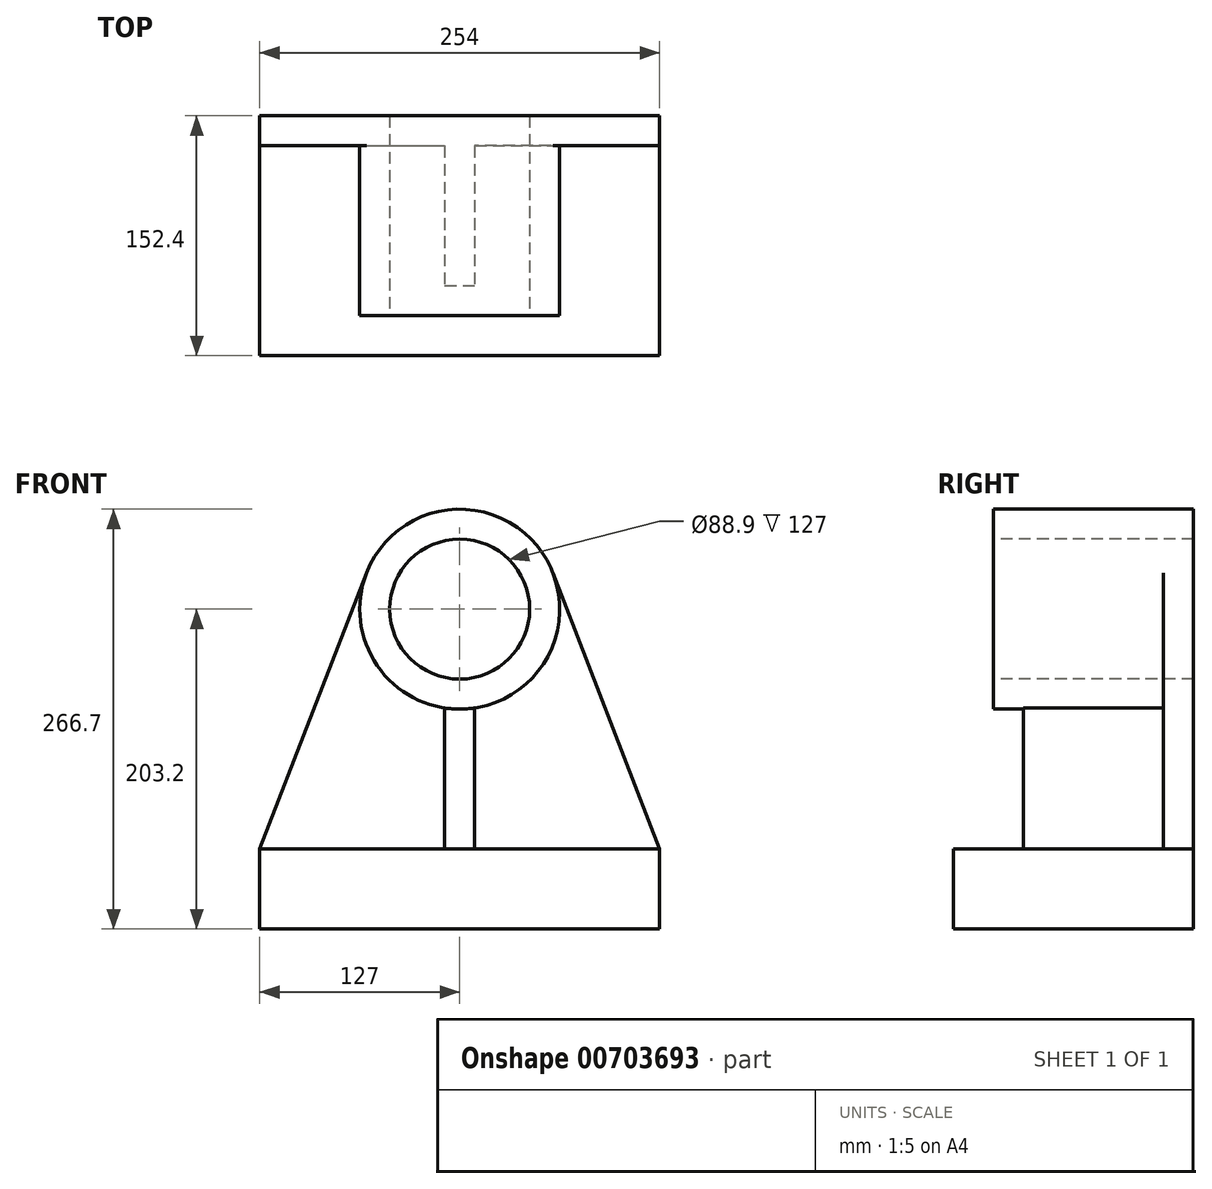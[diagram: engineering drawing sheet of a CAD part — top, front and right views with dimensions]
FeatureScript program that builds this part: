
annotation { "Feature Type Name" : "Feature", "Feature Type Description" : "" }
export const myFeature = defineFeature(function(context is Context, id is Id, definition is map)
    precondition{}
    {
        {
            var Q0;
            Q0=qCreatedBy(makeId("Front.planeOp"),FACE);
            var sketch = newSketch(context, id + "F0", { "sketchPlane" : qUnion([Q0])});
            skLineSegment(sketch, "E0", {"start": v(0, 0) * mm, "end": v(254, 0) * mm});
            skLineSegment(sketch, "E1", {"start": v(254, 0) * mm, "end": v(254, 50.8) * mm});
            skLineSegment(sketch, "E2", {"start": v(254, 50.8) * mm, "end": v(186.23, 226.1) * mm});
            skLineSegment(sketch, "E3", {"start": v(0, 0) * mm, "end": v(0, 50.8) * mm});
            skLineSegment(sketch, "E4", {"start": v(0, 50.8) * mm, "end": v(67.77, 226.1) * mm});
            skArc(sketch, "E5", {"start": v(186.23, 226.1) * mm, "mid": v(127, 266.7) * mm, "end": v(67.77, 226.1) * mm});
            skLineSegment(sketch, "E6", {"start": v(127, 0) * mm, "end": v(127, 266.7) * mm, "construction": true});
            skSolve(sketch);
        }
        {
            var Q0;
            Q0 = qSketchRegion(id + "F0", true);
            extrude(context, id + "F1", {"entities" : qUnion([Q0]), "depth" : 152.4 * mm, "offsetDistance" : 25.4 * mm});
        }
        {
            var Q0;
            Q0=makeQuery(id+"F1.opExtrude","CAP_FACE",FACE,{"disambiguationData":[OSD([sQuery(id+"F0.wireOp",EDGE,"E0"),sQuery(id+"F0.wireOp",EDGE,"E1"),sQuery(id+"F0.wireOp",EDGE,"E2"),sQuery(id+"F0.wireOp",EDGE,"E3"),sQuery(id+"F0.wireOp",EDGE,"E4"),sQuery(id+"F0.wireOp",EDGE,"E5")])],"isStart":false});
            var sketch = newSketch(context, id + "F2", { "sketchPlane" : qUnion([Q0])});
            skLineSegment(sketch, "E7", {"start": v(0, 50.8) * mm, "end": v(117.47, 50.8) * mm});
            skLineSegment(sketch, "E8", {"start": v(117.47, 50.8) * mm, "end": v(117.47, 140.42) * mm});
            skCircle(sketch, "E9", {"center": v(127, 203.2) * mm, "radius": 63.5 * mm});
            skLineSegment(sketch, "E10", {"start": v(254, 50.8) * mm, "end": v(136.53, 50.8) * mm});
            skLineSegment(sketch, "E11", {"start": v(136.53, 50.8) * mm, "end": v(136.53, 140.42) * mm});
            skLineSegment(sketch, "E12", {"start": v(127, 266.7) * mm, "end": v(127, 0) * mm, "construction": true});
            skSolve(sketch);
        }
        {
            var Q0;
            Q0=makeQuery(id+"F2.imprint","IMPRINT",FACE,{"disambiguationData":[TD([[makeQuery(id+"F2.imprint","IMPRINT",EDGE,{"derivedFrom":sQuery(id+"F2.wireOp",EDGE,"E10")}),-1.0]])]});
            var Q1;
            Q1=makeQuery(id+"F2.imprint","IMPRINT",FACE,{"disambiguationData":[TD([[makeQuery(id+"F2.imprint","IMPRINT",EDGE,{"derivedFrom":sQuery(id+"F2.wireOp",EDGE,"E7")}),1.0]])]});
            extrude(context, id + "F3", {"entities" : qUnion([Q0, Q1]), "operationType" : NewBodyOperationType.REMOVE, "oppositeDirection" : true, "depth" : 133.35 * mm, "offsetDistance" : 25.4 * mm});
        }
        {
            var Q0;
            Q0=makeQuery(id+"F1.opExtrude","CAP_FACE",FACE,{"disambiguationData":[OSD([sQuery(id+"F0.wireOp",EDGE,"E0"),sQuery(id+"F0.wireOp",EDGE,"E1"),sQuery(id+"F0.wireOp",EDGE,"E2"),sQuery(id+"F0.wireOp",EDGE,"E3"),sQuery(id+"F0.wireOp",EDGE,"E4"),sQuery(id+"F0.wireOp",EDGE,"E5")])],"isStart":false});
            var sketch = newSketch(context, id + "F4", { "sketchPlane" : qUnion([Q0])});
            skCircle(sketch, "E13", {"center": v(127, 203.2) * mm, "radius": 44.45 * mm});
            skSolve(sketch);
        }
        {
            var Q0;
            Q0 = qSketchRegion(id + "F4", true);
            extrude(context, id + "F5", {"entities" : qUnion([Q0]), "operationType" : NewBodyOperationType.REMOVE, "endBound" : BoundingType.THROUGH_ALL, "oppositeDirection" : true, "depth" : 25.4 * mm, "offsetDistance" : 25.4 * mm});
        }
        {
            var Q0;
            Q0=makeQuery(id+"F1.opExtrude","CAP_FACE",FACE,{"disambiguationData":[OSD([sQuery(id+"F0.wireOp",EDGE,"E0"),sQuery(id+"F0.wireOp",EDGE,"E1"),sQuery(id+"F0.wireOp",EDGE,"E2"),sQuery(id+"F0.wireOp",EDGE,"E3"),sQuery(id+"F0.wireOp",EDGE,"E4"),sQuery(id+"F0.wireOp",EDGE,"E5")])],"isStart":false});
            var sketch = newSketch(context, id + "F6", { "sketchPlane" : qUnion([Q0])});
            skLineSegment(sketch, "E14", {"start": v(117.47, 50.8) * mm, "end": v(136.53, 50.8) * mm});
            skLineSegment(sketch, "E15", {"start": v(136.53, 50.8) * mm, "end": v(136.53, 140.42) * mm});
            skArc(sketch, "E16", {"start": v(117.47, 140.42) * mm, "mid": v(127, 139.7) * mm, "end": v(136.53, 140.42) * mm});
            skLineSegment(sketch, "E17", {"start": v(117.47, 140.42) * mm, "end": v(117.47, 50.8) * mm});
            skSolve(sketch);
        }
        {
            var Q0;
            Q0 = qSketchRegion(id + "F6", true);
            extrude(context, id + "F7", {"entities" : qUnion([Q0]), "operationType" : NewBodyOperationType.REMOVE, "oppositeDirection" : true, "depth" : 44.45 * mm, "offsetDistance" : 25.4 * mm});
        }
        {
            var Q0;
            {var subQ1=sQuery(id+"F0.wireOp",EDGE,"E2");var subQ2=sQuery(id+"F0.wireOp",EDGE,"E4");var subQ3=sQuery(id+"F0.wireOp",EDGE,"E5");Q0=makeQuery(id+"F7.boolean.opBoolean","SPLIT",FACE,{"disambiguationData":[TD([makeQuery(id+"F1.opExtrude","SWEPT_FACE",FACE,{"disambiguationData":[OSD([subQ3])]})])],"derivedFrom":makeQuery(id+"F1.opExtrude","CAP_FACE",FACE,{"disambiguationData":[OSD([sQuery(id+"F0.wireOp",EDGE,"E0"),sQuery(id+"F0.wireOp",EDGE,"E1"),subQ1,sQuery(id+"F0.wireOp",EDGE,"E3"),subQ2,subQ3])],"isStart":false})});}
            var sketch = newSketch(context, id + "F8", { "sketchPlane" : qUnion([Q0])});
            skCircle(sketch, "E18", {"center": v(127, 203.2) * mm, "radius": 44.45 * mm});
            skCircle(sketch, "E19", {"center": v(127, 203.2) * mm, "radius": 63.5 * mm});
            skSolve(sketch);
        }
        {
            var Q0;
            Q0 = qSketchRegion(id + "F8", true);
            extrude(context, id + "F9", {"entities" : qUnion([Q0]), "operationType" : NewBodyOperationType.REMOVE, "oppositeDirection" : true, "depth" : 25.4 * mm, "offsetDistance" : 25.4 * mm});
        }
    });
